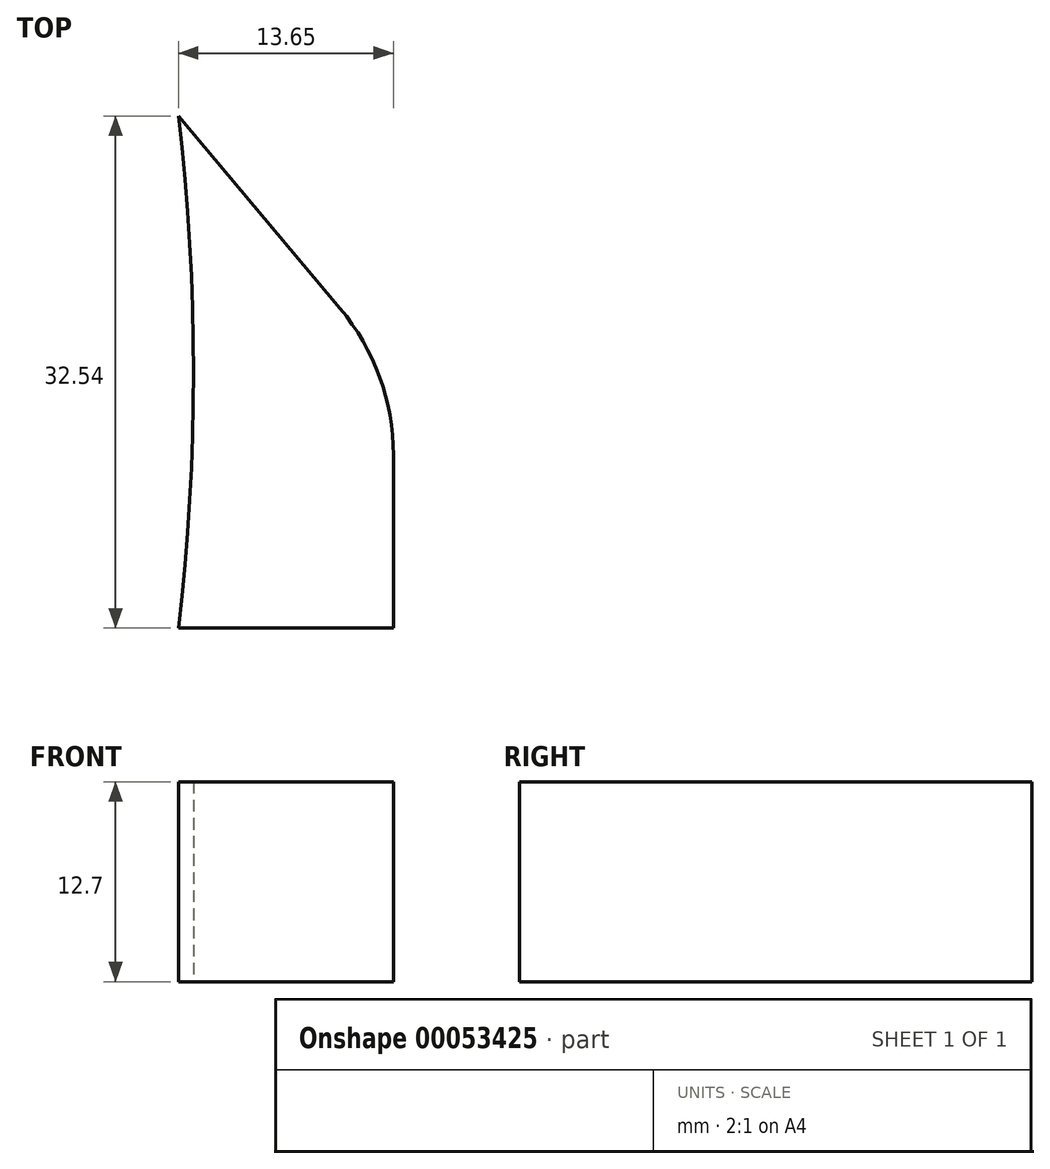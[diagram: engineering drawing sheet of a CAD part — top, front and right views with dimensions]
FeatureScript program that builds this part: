
annotation { "Feature Type Name" : "Feature", "Feature Type Description" : "" }
export const myFeature = defineFeature(function(context is Context, id is Id, definition is map)
    precondition{}
    {
        {
            var Q0;
            Q0=qCreatedBy(makeId("Top.planeOp"),FACE);
            var sketch = newSketch(context, id + "F0", { "sketchPlane" : qUnion([Q0])});
            skCircle(sketch, "E0", {"center": v(-139.7, 0) * mm, "radius": 139.7 * mm});
            skLineSegment(sketch, "E1.rect.bottom", {"start": v(-12.7, -16.27) * mm, "end": v(12.7, -16.27) * mm});
            skLineSegment(sketch, "E1.rect.top", {"start": v(-12.7, 16.27) * mm, "end": v(-0.95, 16.27) * mm});
            skLineSegment(sketch, "E1.rect.left", {"start": v(-12.7, -16.27) * mm, "end": v(-12.7, 16.27) * mm});
            skLineSegment(sketch, "E1.rect.right", {"start": v(12.7, -16.27) * mm, "end": v(12.7, 0) * mm});
            skPoint(sketch, "E1.rect.middle", {"position": v(0, 0) * mm});
            skLineSegment(sketch, "E2", {"start": v(12.7, 0) * mm, "end": v(-0.95, 16.27) * mm});
            skPoint(sketch, "E2.endSnap0", {"position": v(0, 16.27) * mm});
            skPoint(sketch, "E3.orphan", {"position": v(12.7, 16.27) * mm});
            skSolve(sketch);
        }
        {
            var Q0;
            {var subQ4=sQuery(id+"F0.wireOp",EDGE,"E1.rect.right");Q0=makeQuery(id+"F0.imprint","IMPRINT",FACE,{"disambiguationData":[TD([[makeQuery(id+"F0.imprint","IMPRINT",EDGE,{"derivedFrom":subQ4}),1.0]])]});}
            extrude(context, id + "F1", {"entities" : qUnion([Q0]), "depth" : 12.7 * mm});
        }
        {
            var Q0;
            Q0=makeQuery(id+"F1.opExtrude","SWEPT_EDGE",EDGE,{"disambiguationData":[OSD([sQuery(id+"F0.wireOp",EDGE,"E1.rect.right"),sQuery(id+"F0.wireOp",EDGE,"E2")])]});
            fillet(context, id + "F2", {"entities" : qUnion([Q0]), "radius" : 14.47 * mm, "tangentPropagation" : true, "allowEdgeOverflow" : false});
        }
    });
